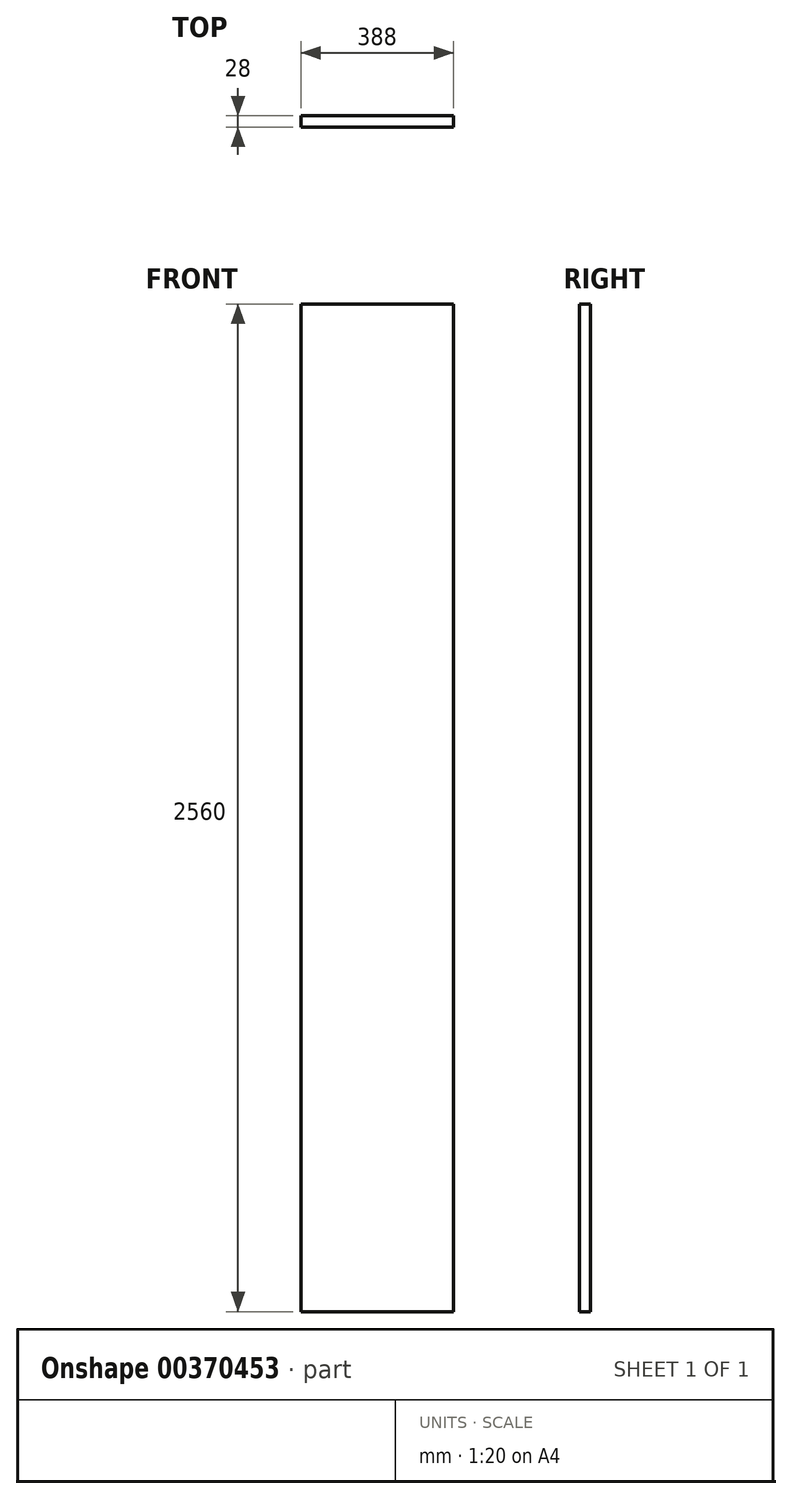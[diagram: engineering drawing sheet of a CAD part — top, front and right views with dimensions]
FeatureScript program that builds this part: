
annotation { "Feature Type Name" : "Feature", "Feature Type Description" : "" }
export const myFeature = defineFeature(function(context is Context, id is Id, definition is map)
    precondition{}
    {
        {
            var Q0;
            Q0=qCreatedBy(makeId("Top.planeOp"),FACE);
            var sketch = newSketch(context, id + "F0", { "sketchPlane" : qUnion([Q0])});
            skLineSegment(sketch, "E0", {"start": v(0, 0) * mm, "end": v(-201.92, 0) * mm});
            skLineSegment(sketch, "E1", {"start": v(-201.92, 0) * mm, "end": v(-201.92, -28) * mm});
            skLineSegment(sketch, "E2", {"start": v(-201.92, -28) * mm, "end": v(186.08, -28) * mm});
            skLineSegment(sketch, "E3", {"start": v(186.08, -28) * mm, "end": v(186.08, 0) * mm});
            skLineSegment(sketch, "E4", {"start": v(186.08, 0) * mm, "end": v(0, 0) * mm});
            skSolve(sketch);
        }
        {
            var Q0;
            Q0=makeQuery(id+"F0.imprint","IMPRINT",FACE,{"disambiguationData":[TD([[makeQuery(id+"F0.imprint","IMPRINT",EDGE,{"derivedFrom":sQuery(id+"F0.wireOp",EDGE,"E0")}),1.0]])]});
            extrude(context, id + "F1", {"entities" : qUnion([Q0]), "depth" : 2560 * mm});
        }
    });
